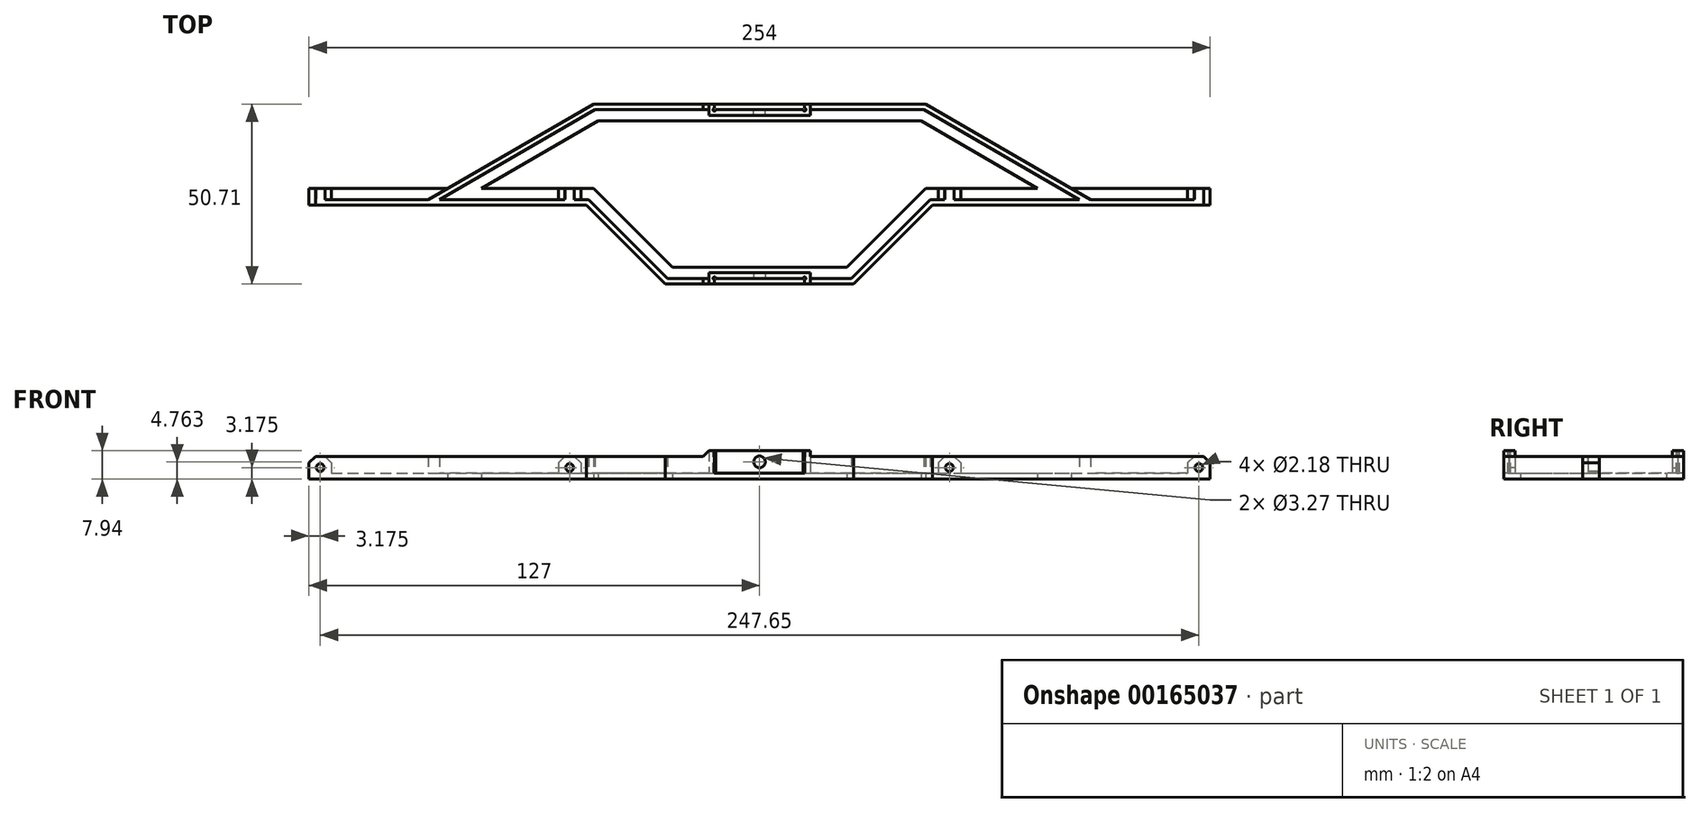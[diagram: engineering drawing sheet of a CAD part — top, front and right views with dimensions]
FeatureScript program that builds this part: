
annotation { "Feature Type Name" : "Feature", "Feature Type Description" : "" }
export const myFeature = defineFeature(function(context is Context, id is Id, definition is map)
    precondition{}
    {
        {
            var Q0;
            Q0=qCreatedBy(makeId("Top.planeOp"),FACE);
            var sketch = newSketch(context, id + "F0", { "sketchPlane" : qUnion([Q0])});
            skLineSegment(sketch, "E0", {"start": v(-127, 22.22) * mm, "end": v(-87.88, 22.22) * mm});
            skLineSegment(sketch, "E1", {"start": v(-46.78, 22.23) * mm, "end": v(-24.56, 0) * mm});
            skLineSegment(sketch, "E2", {"start": v(-24.56, 0) * mm, "end": v(24.56, 0) * mm});
            skLineSegment(sketch, "E3", {"start": v(24.56, 0) * mm, "end": v(46.78, 22.23) * mm});
            skLineSegment(sketch, "E4", {"start": v(87.88, 22.23) * mm, "end": v(127, 22.23) * mm});
            skLineSegment(sketch, "E5", {"start": v(-127, 22.23) * mm, "end": v(-127, 17.46) * mm});
            skLineSegment(sketch, "E6", {"start": v(-127, 17.46) * mm, "end": v(-48.76, 17.46) * mm});
            skLineSegment(sketch, "E7", {"start": v(-48.76, 17.46) * mm, "end": v(-26.53, -4.76) * mm});
            skLineSegment(sketch, "E8", {"start": v(-26.53, -4.76) * mm, "end": v(26.53, -4.76) * mm});
            skLineSegment(sketch, "E9", {"start": v(26.53, -4.76) * mm, "end": v(48.76, 17.46) * mm});
            skLineSegment(sketch, "E10", {"start": v(48.76, 17.46) * mm, "end": v(127, 17.46) * mm});
            skLineSegment(sketch, "E11", {"start": v(127, 17.46) * mm, "end": v(127, 22.23) * mm});
            skLineSegment(sketch, "E12", {"start": v(-35.67, 11.11) * mm, "end": v(-39.04, 7.74) * mm, "construction": true});
            skLineSegment(sketch, "E13", {"start": v(0, 0) * mm, "end": v(0, -4.76) * mm, "construction": true});
            skLineSegment(sketch, "E14", {"start": v(35.67, 11.11) * mm, "end": v(39.04, 7.74) * mm, "construction": true});
            skLineSegment(sketch, "E15", {"start": v(-87.88, 17.46) * mm, "end": v(-87.88, 22.23) * mm, "construction": true});
            skLineSegment(sketch, "E16", {"start": v(87.88, 17.46) * mm, "end": v(87.88, 22.23) * mm, "construction": true});
            skLineSegment(sketch, "E17", {"start": v(-87.88, 22.23) * mm, "end": v(-46.78, 45.95) * mm});
            skLineSegment(sketch, "E18", {"start": v(-78.35, 22.23) * mm, "end": v(-45.5, 41.19) * mm});
            skLineSegment(sketch, "E19", {"start": v(-45.5, 41.19) * mm, "end": v(45.5, 41.19) * mm});
            skLineSegment(sketch, "E20", {"start": v(-46.78, 45.95) * mm, "end": v(46.78, 45.95) * mm});
            skLineSegment(sketch, "E21", {"start": v(-78.35, 22.22) * mm, "end": v(-46.78, 22.22) * mm});
            skLineSegment(sketch, "E22", {"start": v(45.5, 41.19) * mm, "end": v(78.35, 22.22) * mm});
            skLineSegment(sketch, "E23", {"start": v(46.78, 45.95) * mm, "end": v(87.88, 22.22) * mm});
            skLineSegment(sketch, "E24", {"start": v(46.78, 22.23) * mm, "end": v(78.35, 22.23) * mm});
            skLineSegment(sketch, "E25", {"start": v(0, 0) * mm, "end": v(0, 41.19) * mm, "construction": true});
            skLineSegment(sketch, "E26", {"start": v(0, 41.19) * mm, "end": v(0, 45.95) * mm, "construction": true});
            skLineSegment(sketch, "E27", {"start": v(-61.93, 31.7) * mm, "end": v(-64.31, 35.83) * mm, "construction": true});
            skLineSegment(sketch, "E28", {"start": v(61.93, 31.7) * mm, "end": v(64.31, 35.83) * mm, "construction": true});
            skLineSegment(sketch, "E29", {"start": v(-46.78, 22.23) * mm, "end": v(0, 22.23) * mm, "construction": true});
            skLineSegment(sketch, "E30", {"start": v(0, 22.23) * mm, "end": v(46.78, 22.23) * mm, "construction": true});
            skSolve(sketch);
        }
        {
            var Q0;
            Q0=qSketchRegion(id+"F0",true);
            extrude(context, id + "F1", {"entities" : qUnion([Q0]), "depth" : 1.59 * mm});
        }
        {
            var Q0;
            Q0=makeQuery(id+"F1.opExtrude","CAP_FACE",FACE,{"disambiguationData":[OSD([sQuery(id+"F0.wireOp",EDGE,"E0"),sQuery(id+"F0.wireOp",EDGE,"E1"),sQuery(id+"F0.wireOp",EDGE,"E2"),sQuery(id+"F0.wireOp",EDGE,"E3"),sQuery(id+"F0.wireOp",EDGE,"E4"),sQuery(id+"F0.wireOp",EDGE,"E5"),sQuery(id+"F0.wireOp",EDGE,"E6"),sQuery(id+"F0.wireOp",EDGE,"E7"),sQuery(id+"F0.wireOp",EDGE,"E8"),sQuery(id+"F0.wireOp",EDGE,"E9"),sQuery(id+"F0.wireOp",EDGE,"E10"),sQuery(id+"F0.wireOp",EDGE,"E11")])],"isStart":false});
            var sketch = newSketch(context, id + "F2", { "sketchPlane" : qUnion([Q0])});
            skLineSegment(sketch, "E31.bottom", {"start": v(-127, 17.46) * mm, "end": v(-48.76, 17.46) * mm});
            skLineSegment(sketch, "E31.top", {"start": v(-127, 19.05) * mm, "end": v(-93.38, 19.05) * mm});
            skLineSegment(sketch, "E31.left", {"start": v(-127, 17.46) * mm, "end": v(-127, 19.05) * mm});
            skLineSegment(sketch, "E32", {"start": v(-48.76, 17.46) * mm, "end": v(-26.53, -4.76) * mm});
            skLineSegment(sketch, "E33", {"start": v(-26.53, -4.76) * mm, "end": v(26.53, -4.76) * mm});
            skLineSegment(sketch, "E34", {"start": v(26.53, -4.76) * mm, "end": v(48.76, 17.46) * mm});
            skLineSegment(sketch, "E35", {"start": v(48.76, 17.46) * mm, "end": v(127, 17.46) * mm});
            skLineSegment(sketch, "E36", {"start": v(127, 17.46) * mm, "end": v(127, 19.05) * mm});
            skLineSegment(sketch, "E37", {"start": v(127, 19.05) * mm, "end": v(93.38, 19.05) * mm});
            skLineSegment(sketch, "E38", {"start": v(48.1, 19.05) * mm, "end": v(25.87, -3.18) * mm});
            skLineSegment(sketch, "E39", {"start": v(-25.87, -3.18) * mm, "end": v(-48.1, 19.05) * mm});
            skLineSegment(sketch, "E40", {"start": v(-37.64, 6.35) * mm, "end": v(-36.52, 7.47) * mm, "construction": true});
            skLineSegment(sketch, "E41", {"start": v(37.64, 6.35) * mm, "end": v(36.52, 7.47) * mm, "construction": true});
            skLineSegment(sketch, "E42", {"start": v(0, -3.18) * mm, "end": v(0, -4.76) * mm, "construction": true});
            skLineSegment(sketch, "E43", {"start": v(-25.87, -3.18) * mm, "end": v(-14.29, -3.18) * mm});
            skLineSegment(sketch, "E44", {"start": v(25.87, -3.18) * mm, "end": v(14.29, -3.18) * mm});
            skLineSegment(sketch, "E45.bottom", {"start": v(-14.29, -3.18) * mm, "end": v(14.29, -3.18) * mm, "construction": true});
            skLineSegment(sketch, "E45.top", {"start": v(-14.29, -1.59) * mm, "end": v(14.29, -1.59) * mm});
            skLineSegment(sketch, "E45.left", {"start": v(-14.29, -3.18) * mm, "end": v(-14.29, -1.59) * mm});
            skLineSegment(sketch, "E45.right", {"start": v(14.29, -3.17) * mm, "end": v(14.29, -1.59) * mm});
            skLineSegment(sketch, "E46", {"start": v(-46.78, 45.95) * mm, "end": v(-93.38, 19.05) * mm});
            skLineSegment(sketch, "E47", {"start": v(-46.78, 45.95) * mm, "end": v(46.78, 45.95) * mm});
            skLineSegment(sketch, "E48", {"start": v(46.78, 45.95) * mm, "end": v(93.38, 19.05) * mm});
            skLineSegment(sketch, "E49", {"start": v(-67.33, 34.09) * mm, "end": v(-66.54, 32.71) * mm, "construction": true});
            skLineSegment(sketch, "E50", {"start": v(0, 45.95) * mm, "end": v(0, 44.36) * mm, "construction": true});
            skLineSegment(sketch, "E51", {"start": v(67.33, 34.09) * mm, "end": v(66.54, 32.71) * mm, "construction": true});
            skLineSegment(sketch, "E52", {"start": v(-90.2, 19.05) * mm, "end": v(-46.36, 44.36) * mm});
            skLineSegment(sketch, "E53", {"start": v(46.36, 44.36) * mm, "end": v(90.2, 19.05) * mm});
            skLineSegment(sketch, "E54", {"start": v(-48.1, 19.05) * mm, "end": v(-90.2, 19.05) * mm});
            skLineSegment(sketch, "E55", {"start": v(48.1, 19.05) * mm, "end": v(90.2, 19.05) * mm});
            skLineSegment(sketch, "E56.bottom", {"start": v(-14.29, 44.36) * mm, "end": v(14.29, 44.36) * mm, "construction": true});
            skLineSegment(sketch, "E56.top", {"start": v(-14.29, 42.78) * mm, "end": v(14.29, 42.78) * mm});
            skLineSegment(sketch, "E56.left", {"start": v(-14.29, 44.36) * mm, "end": v(-14.29, 42.78) * mm});
            skLineSegment(sketch, "E56.right", {"start": v(14.29, 44.36) * mm, "end": v(14.29, 42.78) * mm});
            skLineSegment(sketch, "E57", {"start": v(-14.29, 44.36) * mm, "end": v(-46.36, 44.36) * mm});
            skLineSegment(sketch, "E58", {"start": v(14.29, 44.36) * mm, "end": v(46.36, 44.36) * mm});
            skSolve(sketch);
        }
        {
            var Q0;
            Q0=makeQuery(id+"F2.imprint","IMPRINT",FACE,{"disambiguationData":[TD([[makeQuery(id+"F2.imprint","IMPRINT",EDGE,{"derivedFrom":sQuery(id+"F2.wireOp",EDGE,"E31.bottom")}),1.0]])]});
            extrude(context, id + "F3", {"entities" : qUnion([Q0]), "operationType" : NewBodyOperationType.ADD, "depth" : 4.76 * mm});
        }
        {
            var Q0;
            Q0=makeQuery(id+"F3.opExtrude","SWEPT_FACE",FACE,{"disambiguationData":[OSD([sQuery(id+"F2.wireOp",EDGE,"E31.top")])]});
            var sketch = newSketch(context, id + "F4", { "sketchPlane" : qUnion([Q0])});
            skLineSegment(sketch, "E59.bottom", {"start": v(-50.34, 6.35) * mm, "end": v(-56.7, 6.35) * mm});
            skLineSegment(sketch, "E59.top", {"start": v(-50.34, 0) * mm, "end": v(-56.7, 0) * mm});
            skLineSegment(sketch, "E59.left", {"start": v(-50.34, 6.35) * mm, "end": v(-50.34, 0) * mm});
            skLineSegment(sketch, "E59.right", {"start": v(-56.7, 6.35) * mm, "end": v(-56.7, 0) * mm});
            skLineSegment(sketch, "E60", {"start": v(-50.34, 3.18) * mm, "end": v(-48.76, 3.18) * mm, "construction": true});
            skLineSegment(sketch, "E61.bottom", {"start": v(-127, 6.35) * mm, "end": v(-120.65, 6.35) * mm});
            skLineSegment(sketch, "E61.top", {"start": v(-127, 0) * mm, "end": v(-120.65, 0) * mm});
            skLineSegment(sketch, "E61.left", {"start": v(-127, 6.35) * mm, "end": v(-127, 0) * mm});
            skLineSegment(sketch, "E61.right", {"start": v(-120.65, 6.35) * mm, "end": v(-120.65, 0) * mm});
            skLineSegment(sketch, "E62.bottom", {"start": v(127, 6.35) * mm, "end": v(120.65, 6.35) * mm});
            skLineSegment(sketch, "E62.top", {"start": v(127, 0) * mm, "end": v(120.65, 0) * mm});
            skLineSegment(sketch, "E62.left", {"start": v(127, 6.35) * mm, "end": v(127, 0) * mm});
            skLineSegment(sketch, "E62.right", {"start": v(120.65, 6.35) * mm, "end": v(120.65, 0) * mm});
            skLineSegment(sketch, "E63.bottom", {"start": v(50.34, 6.35) * mm, "end": v(56.7, 6.35) * mm});
            skLineSegment(sketch, "E63.top", {"start": v(50.34, 0) * mm, "end": v(56.7, 0) * mm});
            skLineSegment(sketch, "E63.left", {"start": v(50.34, 6.35) * mm, "end": v(50.34, 0) * mm});
            skLineSegment(sketch, "E63.right", {"start": v(56.7, 6.35) * mm, "end": v(56.7, 0) * mm});
            skLineSegment(sketch, "E64", {"start": v(120.65, 3.18) * mm, "end": v(56.7, 3.18) * mm, "construction": true});
            skLineSegment(sketch, "E65", {"start": v(-56.7, 3.18) * mm, "end": v(-120.65, 3.17) * mm, "construction": true});
            skSolve(sketch);
        }
        {
            var Q0;
            Q0=qSketchRegion(id+"F4",true);
            var Q1;
            Q1=makeQuery(id+"F1.opExtrude","SWEPT_FACE",FACE,{"disambiguationData":[OSD([sQuery(id+"F0.wireOp",EDGE,"E0")])]});
            extrude(context, id + "F5", {"entities" : qUnion([Q0]), "operationType" : NewBodyOperationType.ADD, "endBound" : BoundingType.UP_TO_SURFACE, "endBoundEntityFace" : qUnion([Q1]), "depth" : 25.4 * mm});
        }
        {
            var Q0;
            Q0=makeQuery(id+"F5.boolean.opBoolean","MERGE",EDGE,{"derivedFrom":[makeQuery(id+"F3.opExtrude","CAP_EDGE",EDGE,{"disambiguationData":[OSD([sQuery(id+"F2.wireOp",EDGE,"E31.left")])],"isStart":false}),makeQuery(id+"F5.opExtrude","SWEPT_EDGE",EDGE,{"disambiguationData":[OSD([sQuery(id+"F4.wireOp",EDGE,"E62.bottom"),sQuery(id+"F4.wireOp",EDGE,"E62.left")])]})]});
            var Q1;
            Q1=makeQuery(id+"F5.opExtrude","SWEPT_EDGE",EDGE,{"disambiguationData":[OSD([sQuery(id+"F2.wireOp",EDGE,"E31.top"),sQuery(id+"F4.wireOp",EDGE,"E62.bottom"),sQuery(id+"F4.wireOp",EDGE,"E62.right")])]});
            var Q2;
            Q2=makeQuery(id+"F5.opExtrude","SWEPT_EDGE",EDGE,{"disambiguationData":[OSD([sQuery(id+"F2.wireOp",EDGE,"E31.top"),sQuery(id+"F4.wireOp",EDGE,"E63.bottom"),sQuery(id+"F4.wireOp",EDGE,"E63.right")])]});
            var Q3;
            Q3=makeQuery(id+"F5.opExtrude","SWEPT_EDGE",EDGE,{"disambiguationData":[OSD([sQuery(id+"F2.wireOp",EDGE,"E31.top"),sQuery(id+"F4.wireOp",EDGE,"E63.bottom"),sQuery(id+"F4.wireOp",EDGE,"E63.left")])]});
            var Q4;
            Q4=makeQuery(id+"F5.opExtrude","SWEPT_EDGE",EDGE,{"disambiguationData":[OSD([sQuery(id+"F4.wireOp",EDGE,"E59.bottom"),sQuery(id+"F4.wireOp",EDGE,"E59.left")])]});
            var Q5;
            Q5=makeQuery(id+"F5.opExtrude","SWEPT_EDGE",EDGE,{"disambiguationData":[OSD([sQuery(id+"F4.wireOp",EDGE,"E59.bottom"),sQuery(id+"F4.wireOp",EDGE,"E59.right")])]});
            var Q6;
            Q6=makeQuery(id+"F5.opExtrude","SWEPT_EDGE",EDGE,{"disambiguationData":[OSD([sQuery(id+"F4.wireOp",EDGE,"E61.bottom"),sQuery(id+"F4.wireOp",EDGE,"E61.right")])]});
            var Q7;
            Q7=makeQuery(id+"F5.boolean.opBoolean","MERGE",EDGE,{"derivedFrom":[makeQuery(id+"F3.opExtrude","CAP_EDGE",EDGE,{"disambiguationData":[OSD([sQuery(id+"F2.wireOp",EDGE,"E36")])],"isStart":false}),makeQuery(id+"F5.opExtrude","SWEPT_EDGE",EDGE,{"disambiguationData":[OSD([sQuery(id+"F4.wireOp",EDGE,"E61.bottom"),sQuery(id+"F4.wireOp",EDGE,"E61.left")])]})]});
            chamfer(context, id + "F6", {"entities" : qUnion([Q0, Q1, Q2, Q3, Q4, Q5, Q6, Q7]), "width" : 1.86 * mm, "tangentPropagation" : true});
        }
        {
            var Q0;
            Q0=makeQuery(id+"F5.boolean.opBoolean","MERGE",FACE,{"derivedFrom":[makeQuery(id+"F3.opExtrude","CAP_FACE",FACE,{"disambiguationData":[OSD([sQuery(id+"F2.wireOp",EDGE,"E31.bottom"),sQuery(id+"F2.wireOp",EDGE,"E31.top"),sQuery(id+"F2.wireOp",EDGE,"E31.left"),sQuery(id+"F2.wireOp",EDGE,"E32"),sQuery(id+"F2.wireOp",EDGE,"E33"),sQuery(id+"F2.wireOp",EDGE,"E34"),sQuery(id+"F2.wireOp",EDGE,"E35"),sQuery(id+"F2.wireOp",EDGE,"E36"),sQuery(id+"F2.wireOp",EDGE,"E37"),sQuery(id+"F2.wireOp",EDGE,"E38"),sQuery(id+"F2.wireOp",EDGE,"E39"),sQuery(id+"F2.wireOp",EDGE,"E43"),sQuery(id+"F2.wireOp",EDGE,"E44"),sQuery(id+"F2.wireOp",EDGE,"E45.top"),sQuery(id+"F2.wireOp",EDGE,"E45.left"),sQuery(id+"F2.wireOp",EDGE,"E45.right")])],"isStart":false}),makeQuery(id+"F5.opExtrude","SWEPT_FACE",FACE,{"disambiguationData":[OSD([sQuery(id+"F4.wireOp",EDGE,"E59.bottom")])]}),makeQuery(id+"F5.opExtrude","SWEPT_FACE",FACE,{"disambiguationData":[OSD([sQuery(id+"F4.wireOp",EDGE,"E61.bottom")])]}),makeQuery(id+"F5.opExtrude","SWEPT_FACE",FACE,{"disambiguationData":[OSD([sQuery(id+"F4.wireOp",EDGE,"E62.bottom")])]}),makeQuery(id+"F5.opExtrude","SWEPT_FACE",FACE,{"disambiguationData":[OSD([sQuery(id+"F4.wireOp",EDGE,"E63.bottom")])]})]});
            var sketch = newSketch(context, id + "F7", { "sketchPlane" : qUnion([Q0])});
            skLineSegment(sketch, "E66.bottom", {"start": v(-14.29, -1.59) * mm, "end": v(14.29, -1.59) * mm});
            skLineSegment(sketch, "E66.top", {"start": v(-14.29, -4.76) * mm, "end": v(14.29, -4.76) * mm});
            skLineSegment(sketch, "E66.left", {"start": v(-14.29, -1.59) * mm, "end": v(-14.29, -4.76) * mm});
            skLineSegment(sketch, "E66.right", {"start": v(14.29, -1.59) * mm, "end": v(14.29, -4.76) * mm});
            skLineSegment(sketch, "E67.bottom", {"start": v(-14.29, 42.78) * mm, "end": v(14.29, 42.78) * mm});
            skLineSegment(sketch, "E67.top", {"start": v(-14.29, 45.95) * mm, "end": v(14.29, 45.95) * mm});
            skLineSegment(sketch, "E67.left", {"start": v(-14.29, 42.78) * mm, "end": v(-14.29, 45.95) * mm});
            skLineSegment(sketch, "E67.right", {"start": v(14.29, 42.78) * mm, "end": v(14.29, 45.95) * mm});
            skSolve(sketch);
        }
        {
            var Q0;
            Q0=qSketchRegion(id+"F7",true);
            extrude(context, id + "F8", {"entities" : qUnion([Q0]), "operationType" : NewBodyOperationType.ADD, "depth" : 1.59 * mm});
        }
        {
            var Q0;
            Q0=makeQuery(id+"F8.opExtrude","CAP_FACE",FACE,{"disambiguationData":[OSD([sQuery(id+"F7.wireOp",EDGE,"E67.bottom"),sQuery(id+"F7.wireOp",EDGE,"E67.top"),sQuery(id+"F7.wireOp",EDGE,"E67.left"),sQuery(id+"F7.wireOp",EDGE,"E67.right")])],"isStart":false});
            var sketch = newSketch(context, id + "F9", { "sketchPlane" : qUnion([Q0])});
            skLineSegment(sketch, "E68.bottom", {"start": v(-12.7, -4.76) * mm, "end": v(12.7, -4.76) * mm});
            skLineSegment(sketch, "E68.top", {"start": v(-12.7, -3.18) * mm, "end": v(12.7, -3.18) * mm});
            skLineSegment(sketch, "E68.left", {"start": v(-12.7, -4.76) * mm, "end": v(-12.7, -3.18) * mm});
            skLineSegment(sketch, "E68.right", {"start": v(12.7, -4.76) * mm, "end": v(12.7, -3.18) * mm});
            skLineSegment(sketch, "E69.bottom", {"start": v(-12.7, -3.18) * mm, "end": v(-14.29, -3.18) * mm, "construction": true});
            skLineSegment(sketch, "E69.top", {"start": v(-12.7, -1.59) * mm, "end": v(-14.29, -1.59) * mm, "construction": true});
            skLineSegment(sketch, "E69.left", {"start": v(-12.7, -3.18) * mm, "end": v(-12.7, -1.59) * mm, "construction": true});
            skLineSegment(sketch, "E69.right", {"start": v(-14.29, -3.18) * mm, "end": v(-14.29, -1.59) * mm, "construction": true});
            skLineSegment(sketch, "E70.bottom", {"start": v(12.7, -3.18) * mm, "end": v(14.29, -3.18) * mm, "construction": true});
            skLineSegment(sketch, "E70.top", {"start": v(12.7, -1.59) * mm, "end": v(14.29, -1.59) * mm, "construction": true});
            skLineSegment(sketch, "E70.left", {"start": v(12.7, -3.18) * mm, "end": v(12.7, -1.59) * mm, "construction": true});
            skLineSegment(sketch, "E70.right", {"start": v(14.29, -3.18) * mm, "end": v(14.29, -1.59) * mm, "construction": true});
            skLineSegment(sketch, "E71.bottom", {"start": v(-14.29, 42.78) * mm, "end": v(-12.7, 42.78) * mm, "construction": true});
            skLineSegment(sketch, "E71.top", {"start": v(-14.29, 44.36) * mm, "end": v(-12.7, 44.36) * mm, "construction": true});
            skLineSegment(sketch, "E71.left", {"start": v(-14.29, 42.78) * mm, "end": v(-14.29, 44.36) * mm, "construction": true});
            skLineSegment(sketch, "E71.right", {"start": v(-12.7, 42.78) * mm, "end": v(-12.7, 44.36) * mm, "construction": true});
            skLineSegment(sketch, "E72.bottom", {"start": v(14.29, 44.36) * mm, "end": v(12.7, 44.36) * mm, "construction": true});
            skLineSegment(sketch, "E72.top", {"start": v(14.29, 42.78) * mm, "end": v(12.7, 42.78) * mm, "construction": true});
            skLineSegment(sketch, "E72.left", {"start": v(14.29, 44.36) * mm, "end": v(14.29, 42.78) * mm, "construction": true});
            skLineSegment(sketch, "E72.right", {"start": v(12.7, 44.36) * mm, "end": v(12.7, 42.78) * mm, "construction": true});
            skLineSegment(sketch, "E73.bottom", {"start": v(-12.7, 44.36) * mm, "end": v(12.7, 44.36) * mm});
            skLineSegment(sketch, "E73.top", {"start": v(-12.7, 45.95) * mm, "end": v(12.7, 45.95) * mm});
            skLineSegment(sketch, "E73.left", {"start": v(-12.7, 44.36) * mm, "end": v(-12.7, 45.95) * mm});
            skLineSegment(sketch, "E73.right", {"start": v(12.7, 44.36) * mm, "end": v(12.7, 45.95) * mm});
            skSolve(sketch);
        }
        {
            var Q0;
            Q0=qSketchRegion(id+"F9",true);
            var Q1;
            {var subQ2=sQuery(id+"F0.wireOp",EDGE,"E0");var subQ3=sQuery(id+"F0.wireOp",EDGE,"E24");var subQ7=sQuery(id+"F0.wireOp",EDGE,"E21");var subQ9=sQuery(id+"F0.wireOp",EDGE,"E18");var subQ10=makeQuery(id+"F1.opExtrude","SWEPT_FACE",FACE,{"disambiguationData":[OSD([subQ9])]});var subQ12=sQuery(id+"F0.wireOp",EDGE,"E19");var subQ15=sQuery(id+"F0.wireOp",EDGE,"E22");var subQ22=sQuery(id+"F0.wireOp",EDGE,"E2");var subQ23=sQuery(id+"F0.wireOp",EDGE,"E3");var subQ24=sQuery(id+"F0.wireOp",EDGE,"E1");Q1=makeQuery(id+"F5.boolean.opBoolean","SPLIT",FACE,{"disambiguationData":[TD([subQ10])],"derivedFrom":makeQuery(id+"F3.boolean.opBoolean","SPLIT",FACE,{"disambiguationData":[TD([makeQuery(id+"F1.opExtrude","SWEPT_FACE",FACE,{"disambiguationData":[OSD([subQ24])]})])],"derivedFrom":makeQuery(id+"F1.opExtrude","CAP_FACE",FACE,{"disambiguationData":[OSD([subQ2,subQ24,subQ22,subQ23,sQuery(id+"F0.wireOp",EDGE,"E4"),sQuery(id+"F0.wireOp",EDGE,"E5"),sQuery(id+"F0.wireOp",EDGE,"E6"),sQuery(id+"F0.wireOp",EDGE,"E7"),sQuery(id+"F0.wireOp",EDGE,"E8"),sQuery(id+"F0.wireOp",EDGE,"E9"),sQuery(id+"F0.wireOp",EDGE,"E10"),sQuery(id+"F0.wireOp",EDGE,"E11"),sQuery(id+"F0.wireOp",EDGE,"E17"),subQ9,subQ12,sQuery(id+"F0.wireOp",EDGE,"E20"),subQ7,subQ15,sQuery(id+"F0.wireOp",EDGE,"E23"),subQ3])],"isStart":false})})});}
            extrude(context, id + "F10", {"entities" : qUnion([Q0]), "operationType" : NewBodyOperationType.REMOVE, "endBound" : BoundingType.UP_TO_SURFACE, "oppositeDirection" : true, "endBoundEntityFace" : qUnion([Q1]), "depth" : 25.4 * mm});
        }
        {
            var Q0;
            Q0=makeQuery(id+"F10.boolean.opBoolean","COPY",FACE,{"derivedFrom":makeQuery(id+"F10.opExtrude","SWEPT_FACE",FACE,{"disambiguationData":[OSD([sQuery(id+"F9.wireOp",EDGE,"E68.top")])]})});
            var sketch = newSketch(context, id + "F11", { "sketchPlane" : qUnion([Q0])});
            skLineSegment(sketch, "E74", {"start": v(123.82, 6.35) * mm, "end": v(123.82, 0) * mm, "construction": true});
            skLineSegment(sketch, "E75", {"start": v(53.52, 6.35) * mm, "end": v(53.52, 0) * mm, "construction": true});
            skCircle(sketch, "E76", {"center": v(53.52, 3.17) * mm, "radius": 1.1 * mm});
            skCircle(sketch, "E77", {"center": v(123.82, 3.18) * mm, "radius": 1.1 * mm});
            skLineSegment(sketch, "E78", {"start": v(-53.52, 6.35) * mm, "end": v(-53.52, 0) * mm, "construction": true});
            skLineSegment(sketch, "E79", {"start": v(-123.82, 6.35) * mm, "end": v(-123.82, 0) * mm, "construction": true});
            skCircle(sketch, "E80", {"center": v(-123.82, 3.18) * mm, "radius": 1.1 * mm});
            skCircle(sketch, "E81", {"center": v(-53.52, 3.18) * mm, "radius": 1.1 * mm});
            skLineSegment(sketch, "E82", {"start": v(0, 7.94) * mm, "end": v(0, 4.76) * mm, "construction": true});
            skCircle(sketch, "E83", {"center": v(0, 4.76) * mm, "radius": 1.63 * mm});
            skSolve(sketch);
        }
        {
            var Q0;
            Q0=qSketchRegion(id+"F11",true);
            var Q1;
            Q1=makeQuery(id+"F5.boolean.opBoolean","MERGE",FACE,{"derivedFrom":[makeQuery(id+"F1.opExtrude","SWEPT_FACE",FACE,{"disambiguationData":[OSD([sQuery(id+"F0.wireOp",EDGE,"E21")])]}),makeQuery(id+"F5.opExtrude","CAP_FACE",FACE,{"disambiguationData":[OSD([sQuery(id+"F0.wireOp",EDGE,"E0")]),ownerDisambiguation([makeQuery(id+"F5.opExtrude","SWEPT_BODY",BODY,{"disambiguationData":[OSD([sQuery(id+"F4.wireOp",EDGE,"E63.bottom"),sQuery(id+"F4.wireOp",EDGE,"E63.top"),sQuery(id+"F4.wireOp",EDGE,"E63.left"),sQuery(id+"F4.wireOp",EDGE,"E63.right")])]})])],"isStart":false})]});
            extrude(context, id + "F12", {"entities" : qUnion([Q0]), "operationType" : NewBodyOperationType.REMOVE, "endBound" : BoundingType.UP_TO_SURFACE, "oppositeDirection" : true, "endBoundEntityFace" : qUnion([Q1]), "depth" : 25.4 * mm});
        }
        {
            var Q0;
            Q0=makeQuery(id+"F8.opExtrude","CAP_EDGE",EDGE,{"disambiguationData":[OSD([sQuery(id+"F7.wireOp",EDGE,"E66.left")])],"isStart":true});
            var Q1;
            Q1=makeQuery(id+"F8.opExtrude","CAP_EDGE",EDGE,{"disambiguationData":[OSD([sQuery(id+"F7.wireOp",EDGE,"E66.right")])],"isStart":true});
            var Q2;
            Q2=makeQuery(id+"F8.opExtrude","CAP_EDGE",EDGE,{"disambiguationData":[OSD([sQuery(id+"F7.wireOp",EDGE,"E67.left")])],"isStart":true});
            var Q3;
            Q3=makeQuery(id+"F8.opExtrude","CAP_EDGE",EDGE,{"disambiguationData":[OSD([sQuery(id+"F7.wireOp",EDGE,"E67.right")])],"isStart":true});
            chamfer(context, id + "F13", {"entities" : qUnion([Q0, Q1, Q2, Q3]), "width" : 1.59 * mm, "tangentPropagation" : true});
        }
        {
            var Q0;
            Q0=makeQuery(id+"F8.opExtrude","CAP_FACE",FACE,{"disambiguationData":[OSD([sQuery(id+"F7.wireOp",EDGE,"E67.bottom"),sQuery(id+"F7.wireOp",EDGE,"E67.top"),sQuery(id+"F7.wireOp",EDGE,"E67.left"),sQuery(id+"F7.wireOp",EDGE,"E67.right")])],"isStart":false});
            var sketch = newSketch(context, id + "F14", { "sketchPlane" : qUnion([Q0])});
            skCircle(sketch, "E84", {"center": v(-12.7, -3.18) * mm, "radius": 0.4 * mm});
            skCircle(sketch, "E85", {"center": v(12.7, -3.18) * mm, "radius": 0.4 * mm});
            skCircle(sketch, "E86", {"center": v(-12.7, 44.36) * mm, "radius": 0.4 * mm});
            skCircle(sketch, "E87", {"center": v(12.7, 44.36) * mm, "radius": 0.4 * mm});
            skSolve(sketch);
        }
        {
            var Q0;
            Q0=qSketchRegion(id+"F14",true);
            var Q1;
            Q1=makeQuery(id+"F10.boolean.opBoolean","COPY",FACE,{"derivedFrom":makeQuery(id+"F10.opExtrude","CAP_FACE",FACE,{"disambiguationData":[OSD([sQuery(id+"F9.wireOp",EDGE,"E68.bottom"),sQuery(id+"F9.wireOp",EDGE,"E68.top"),sQuery(id+"F9.wireOp",EDGE,"E68.left"),sQuery(id+"F9.wireOp",EDGE,"E68.right")])],"isStart":false})});
            extrude(context, id + "F15", {"entities" : qUnion([Q0]), "operationType" : NewBodyOperationType.REMOVE, "endBound" : BoundingType.UP_TO_SURFACE, "oppositeDirection" : true, "endBoundEntityFace" : qUnion([Q1]), "depth" : 25.4 * mm});
        }
        {
            var Q0;
            Q0=makeQuery(id+"F10.boolean.opBoolean","COPY",FACE,{"derivedFrom":makeQuery(id+"F10.opExtrude","SWEPT_FACE",FACE,{"disambiguationData":[OSD([sQuery(id+"F9.wireOp",EDGE,"E73.bottom")])]})});
            var sketch = newSketch(context, id + "F16", { "sketchPlane" : qUnion([Q0])});
            skCircle(sketch, "E88", {"center": v(0, 4.76) * mm, "radius": 1.63 * mm});
            skSolve(sketch);
        }
        {
            var Q0;
            Q0=makeQuery(id+"F16.imprint","IMPRINT",FACE,{"disambiguationData":[TD([[makeQuery(id+"F16.imprint","IMPRINT",EDGE,{"derivedFrom":sQuery(id+"F16.wireOp",EDGE,"E88")}),1.0]])]});
            var Q1;
            Q1=makeQuery(id+"F8.boolean.opBoolean","MERGE",FACE,{"derivedFrom":[makeQuery(id+"F3.opExtrude","SWEPT_FACE",FACE,{"disambiguationData":[OSD([sQuery(id+"F2.wireOp",EDGE,"E56.top")])]}),makeQuery(id+"F8.opExtrude","SWEPT_FACE",FACE,{"disambiguationData":[OSD([sQuery(id+"F7.wireOp",EDGE,"E67.bottom")])]})]});
            extrude(context, id + "F17", {"entities" : qUnion([Q0]), "operationType" : NewBodyOperationType.REMOVE, "endBound" : BoundingType.UP_TO_SURFACE, "oppositeDirection" : true, "endBoundEntityFace" : qUnion([Q1]), "depth" : 25.4 * mm});
        }
    });
